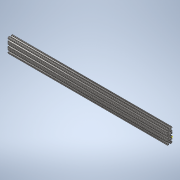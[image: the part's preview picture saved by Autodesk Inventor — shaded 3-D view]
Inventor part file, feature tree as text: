
AUTODESK INVENTOR PART (.ipt)
format: ipt  version: 2020 (Build 240168000, 168)  size: 395,264 bytes
history: native  units: in
note: dims shown in document units (in); Inventor stores cm internally (conversion verified against a paired STEP export)
features: sketch x2, extrude x1
ambient origin geometry x8: Origin, YZ Plane, XZ Plane, XY Plane, X Axis, Y Axis, Z Axis, Center Point
bodies: Solid1 (feature_tree)
feature tree (3):
  extrude  "Extrusion1"  [1 undecoded]
  sketch  "Sketch2"
  sketch  "Sketch1"  dims[d0=33.0in d1=0.0in]
note: 1 required parameter value undecoded (feature->parameter linkage not recoverable at this tier; creation-order binding heuristic only, values carry confidence <= 0.55)
